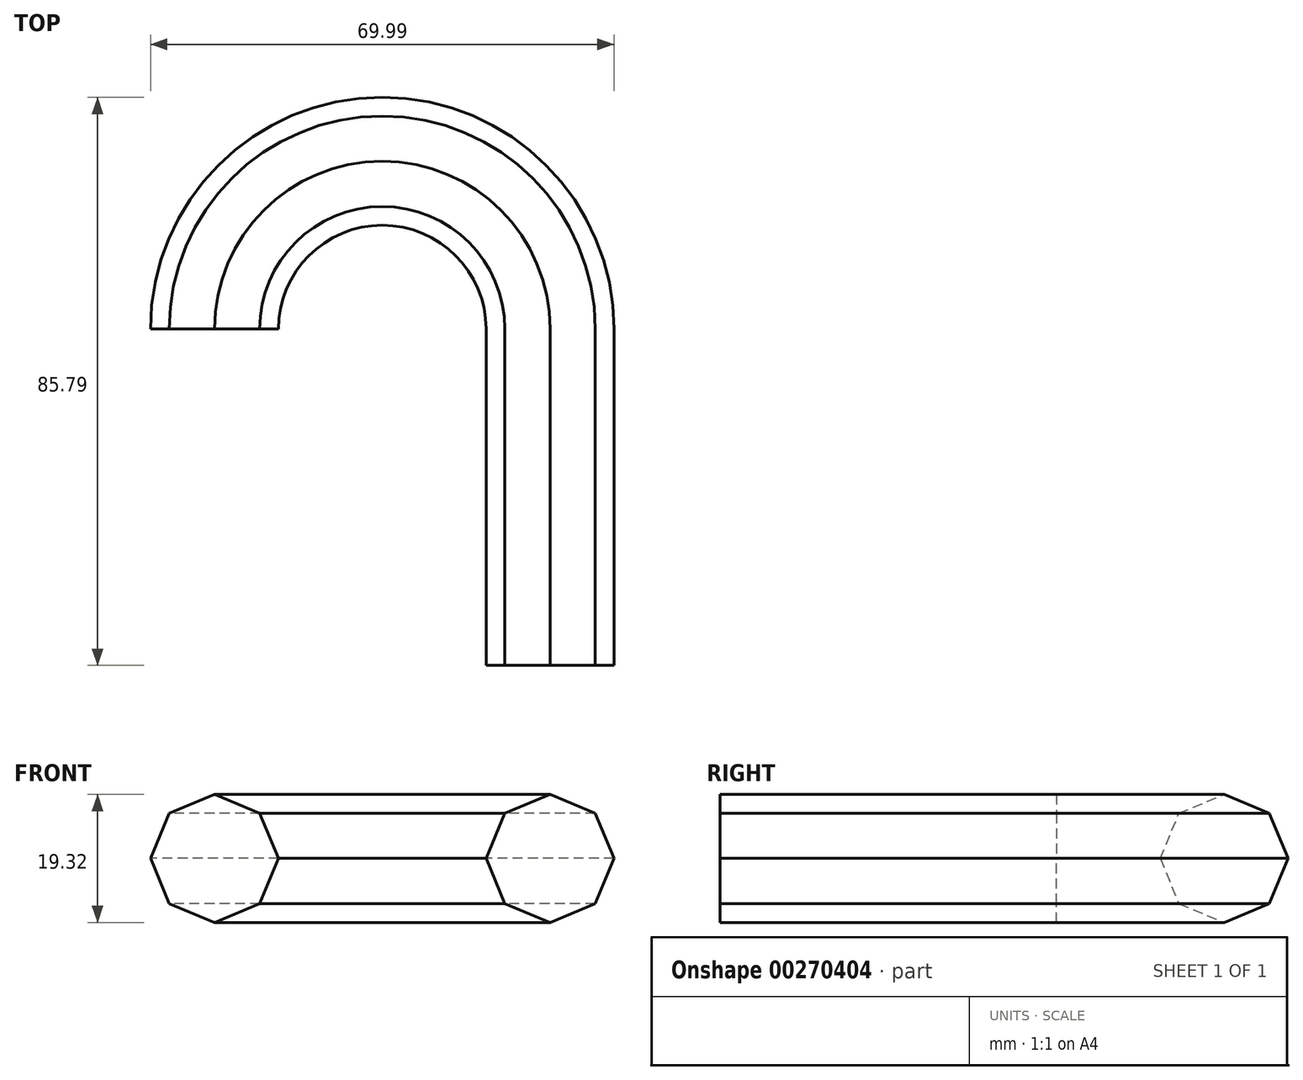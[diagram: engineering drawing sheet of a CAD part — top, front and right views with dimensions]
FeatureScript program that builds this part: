
annotation { "Feature Type Name" : "Feature", "Feature Type Description" : "" }
export const myFeature = defineFeature(function(context is Context, id is Id, definition is map)
    precondition{}
    {
        {
            var Q0;
            Q0=qCreatedBy(makeId("Top.planeOp"),FACE);
            var sketch = newSketch(context, id + "F0", { "sketchPlane" : qUnion([Q0])});
            skLineSegment(sketch, "E0", {"start": v(0, 0) * mm, "end": v(0, 50.8) * mm});
            skArc(sketch, "E1", {"start": v(0, 50.8) * mm, "mid": v(-25.34, 76.14) * mm, "end": v(-50.67, 50.8) * mm});
            skSolve(sketch);
        }
        {
            var Q0;
            Q0=qCreatedBy(makeId("Front.planeOp"),FACE);
            var sketch = newSketch(context, id + "F1", { "sketchPlane" : qUnion([Q0])});
            skCircle(sketch, "E2.cCircle", {"center": v(0, 0) * mm, "radius": 9.66 * mm, "construction": true});
            skLineSegment(sketch, "E2.0", {"start": v(0, 9.66) * mm, "end": v(6.83, 6.83) * mm});
            skLineSegment(sketch, "E2.1", {"start": v(6.83, 6.83) * mm, "end": v(9.66, 0) * mm});
            skLineSegment(sketch, "E2.2", {"start": v(9.66, 0) * mm, "end": v(6.83, -6.83) * mm});
            skLineSegment(sketch, "E2.3", {"start": v(6.83, -6.83) * mm, "end": v(0, -9.66) * mm});
            skLineSegment(sketch, "E2.4", {"start": v(0, -9.66) * mm, "end": v(-6.83, -6.83) * mm});
            skLineSegment(sketch, "E2.5", {"start": v(-6.83, -6.83) * mm, "end": v(-9.66, 0) * mm});
            skLineSegment(sketch, "E2.6", {"start": v(-9.66, 0) * mm, "end": v(-6.83, 6.83) * mm});
            skLineSegment(sketch, "E2.7", {"start": v(-6.83, 6.83) * mm, "end": v(0, 9.66) * mm});
            skSolve(sketch);
        }
        {
            var Q0;
            Q0=makeQuery(id+"F1.imprint","IMPRINT",FACE,{"disambiguationData":[TD([[makeQuery(id+"F1.imprint","IMPRINT",EDGE,{"derivedFrom":sQuery(id+"F1.wireOp",EDGE,"E2.0")}),-1.0]])]});
            var Q1;
            Q1=sQuery(id+"F0.wireOp",EDGE,"E0");
            var Q2;
            Q2=sQuery(id+"F0.wireOp",EDGE,"E1");
            sweep(context, id + "F2", {"profiles" : qUnion([Q0]), "path" : qUnion([Q1, Q2])});
        }
    });
